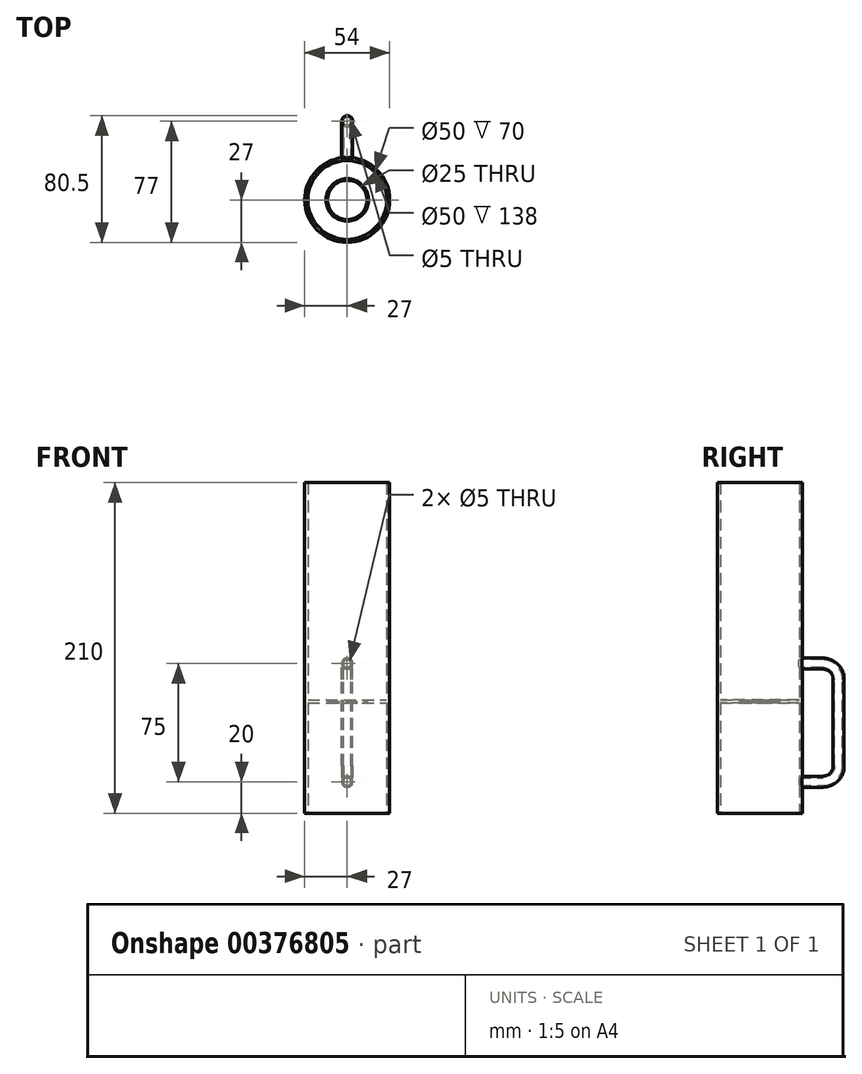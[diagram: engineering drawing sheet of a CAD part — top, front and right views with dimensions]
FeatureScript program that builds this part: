
annotation { "Feature Type Name" : "Feature", "Feature Type Description" : "" }
export const myFeature = defineFeature(function(context is Context, id is Id, definition is map)
    precondition{}
    {
        {
            var Q0;
            Q0=qCreatedBy(makeId("Front.planeOp"),FACE);
            var sketch = newSketch(context, id + "F0", { "sketchPlane" : qUnion([Q0])});
            skLineSegment(sketch, "E0", {"start": v(-27, 210) * mm, "end": v(-27, 0) * mm});
            skLineSegment(sketch, "E1", {"start": v(-27, 0) * mm, "end": v(-25, 0) * mm});
            skLineSegment(sketch, "E2", {"start": v(-25, 0) * mm, "end": v(-25, 70) * mm});
            skLineSegment(sketch, "E3", {"start": v(-25, 70) * mm, "end": v(-12.5, 70) * mm});
            skLineSegment(sketch, "E4", {"start": v(-12.5, 70) * mm, "end": v(-12.5, 71) * mm});
            skLineSegment(sketch, "E5", {"start": v(-12.5, 71) * mm, "end": v(-13.5, 72) * mm});
            skLineSegment(sketch, "E6", {"start": v(-13.5, 72) * mm, "end": v(-25, 72) * mm});
            skLineSegment(sketch, "E7", {"start": v(-25, 72) * mm, "end": v(-25, 210) * mm});
            skLineSegment(sketch, "E8", {"start": v(-25, 210) * mm, "end": v(-27, 210) * mm});
            skLineSegment(sketch, "E9", {"start": v(0, 0) * mm, "end": v(0, 210) * mm, "construction": true});
            skSolve(sketch);
        }
        {
            var Q0;
            Q0 = qSketchRegion(id + "F0", true);
            var Q1;
            Q1=sQuery(id+"F0.wireOp",EDGE,"E9");
            revolve(context, id + "F1", {"entities" : qUnion([Q0]), "axis" : qUnion([Q1]), "revolveType" : RevolveType.FULL});
        }
        {
            var Q0;
            Q0=qCreatedBy(makeId("Right.planeOp"),FACE);
            var sketch = newSketch(context, id + "F2", { "sketchPlane" : qUnion([Q0])});
            skLineSegment(sketch, "E10", {"start": v(0, 20) * mm, "end": v(40, 20) * mm});
            skLineSegment(sketch, "E11", {"start": v(50, 30) * mm, "end": v(50, 85) * mm});
            skLineSegment(sketch, "E12", {"start": v(40, 95) * mm, "end": v(0, 95) * mm});
            skPoint(sketch, "E13.visualSharp", {"position": v(50, 95) * mm});
            skArc(sketch, "E13.filletArc", {"start": v(50, 85) * mm, "mid": v(47.07, 92.07) * mm, "end": v(40, 95) * mm});
            skPoint(sketch, "E14.visualSharp", {"position": v(50, 20) * mm});
            skArc(sketch, "E14.filletArc", {"start": v(40, 20) * mm, "mid": v(47.07, 22.93) * mm, "end": v(50, 30) * mm});
            skSolve(sketch);
        }
        {
            var Q0;
            Q0=qCreatedBy(makeId("Front.planeOp"),FACE);
            var sketch = newSketch(context, id + "F3", { "sketchPlane" : qUnion([Q0])});
            skCircle(sketch, "E15", {"center": v(0, 20) * mm, "radius": 3.5 * mm});
            skSolve(sketch);
        }
        {
            var Q0;
            Q0=makeQuery(id+"F3.imprint","IMPRINT",FACE,{"disambiguationData":[TD([[makeQuery(id+"F3.imprint","IMPRINT",EDGE,{"derivedFrom":sQuery(id+"F3.wireOp",EDGE,"E15")}),1.0]])]});
            var Q1;
            Q1=sQuery(id+"F3.wireOp",EDGE,"E15");
            var Q2;
            Q2=sQuery(id+"F2.wireOp",EDGE,"E10");
            var Q3;
            Q3=sQuery(id+"F2.wireOp",EDGE,"E14.filletArc");
            var Q4;
            Q4=sQuery(id+"F2.wireOp",EDGE,"E11");
            var Q5;
            Q5=sQuery(id+"F2.wireOp",EDGE,"E13.filletArc");
            var Q6;
            Q6=sQuery(id+"F2.wireOp",EDGE,"E12");
            sweep(context, id + "F4", {"operationType" : NewBodyOperationType.ADD, "profiles" : qUnion([Q0]), "surfaceProfiles" : qUnion([Q1]), "path" : qUnion([Q2, Q3, Q4, Q5, Q6])});
        }
        {
            var Q0;
            Q0=qCreatedBy(makeId("Front.planeOp"),FACE);
            var sketch = newSketch(context, id + "F5", { "sketchPlane" : qUnion([Q0])});
            skCircle(sketch, "E16", {"center": v(0, 20) * mm, "radius": 2.5 * mm});
            skSolve(sketch);
        }
        {
            var Q0;
            Q0=makeQuery(id+"F5.imprint","IMPRINT",FACE,{"disambiguationData":[TD([[makeQuery(id+"F5.imprint","IMPRINT",EDGE,{"derivedFrom":sQuery(id+"F5.wireOp",EDGE,"E16")}),1.0]])]});
            var Q1;
            Q1=sQuery(id+"F2.wireOp",EDGE,"E10");
            var Q2;
            Q2=sQuery(id+"F2.wireOp",EDGE,"E14.filletArc");
            var Q3;
            Q3=sQuery(id+"F2.wireOp",EDGE,"E11");
            var Q4;
            Q4=sQuery(id+"F2.wireOp",EDGE,"E13.filletArc");
            var Q5;
            Q5=sQuery(id+"F2.wireOp",EDGE,"E12");
            sweep(context, id + "F6", {"operationType" : NewBodyOperationType.REMOVE, "profiles" : qUnion([Q0]), "path" : qUnion([Q1, Q2, Q3, Q4, Q5])});
        }
        {
            var Q0;
            Q0=makeQuery(id+"F1.opRevolve","SWEPT_FACE",FACE,{"disambiguationData":[OSD([sQuery(id+"F0.wireOp",EDGE,"E8")])]});
            var sketch = newSketch(context, id + "F7", { "sketchPlane" : qUnion([Q0])});
            skCircle(sketch, "E17", {"center": v(0, 0) * mm, "radius": 25 * mm});
            skSolve(sketch);
        }
        {
            var Q0;
            Q0 = qSketchRegion(id + "F7", true);
            var Q1;
            Q1=makeQuery(id+"F1.opRevolve","SWEPT_FACE",FACE,{"disambiguationData":[OSD([sQuery(id+"F0.wireOp",EDGE,"E6")])]});
            extrude(context, id + "F8", {"entities" : qUnion([Q0]), "operationType" : NewBodyOperationType.REMOVE, "endBound" : BoundingType.UP_TO_SURFACE, "oppositeDirection" : true, "endBoundEntityFace" : qUnion([Q1]), "depth" : 25 * mm});
        }
        {
            var Q0;
            Q0=makeQuery(id+"F1.opRevolve","SWEPT_FACE",FACE,{"disambiguationData":[OSD([sQuery(id+"F0.wireOp",EDGE,"E1")])]});
            var sketch = newSketch(context, id + "F9", { "sketchPlane" : qUnion([Q0])});
            skCircle(sketch, "E18", {"center": v(0, 0) * mm, "radius": 25 * mm});
            skSolve(sketch);
        }
        {
            var Q0;
            Q0 = qSketchRegion(id + "F9", true);
            var Q1;
            Q1=makeQuery(id+"F1.opRevolve","SWEPT_FACE",FACE,{"disambiguationData":[OSD([sQuery(id+"F0.wireOp",EDGE,"E3")])]});
            extrude(context, id + "F10", {"entities" : qUnion([Q0]), "operationType" : NewBodyOperationType.REMOVE, "endBound" : BoundingType.UP_TO_SURFACE, "oppositeDirection" : true, "endBoundEntityFace" : qUnion([Q1]), "depth" : 25 * mm});
        }
    });
